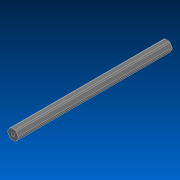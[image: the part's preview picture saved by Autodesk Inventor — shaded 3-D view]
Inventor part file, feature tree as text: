
AUTODESK INVENTOR PART (.ipt)
format: ipt  version: 2022.2 (Build 262287000, 287)  size: 122,368 bytes
history: native  units: in
note: dims shown in document units (in); Inventor stores cm internally (conversion verified against a paired STEP export)
features: extrude x1, sketch x1, other x1
ambient origin geometry x8: Origin, YZ Plane, XZ Plane, XY Plane, X Axis, Y Axis, Z Axis, Center Point
bodies: Solid1 (feature_tree)
feature tree (3):
  extrude  "Extrusion1"  TaperAngle=0.0deg  [1 undecoded]
  sketch  "Sketch1"  dims[d0=28.0in d1=0.0in]
  other  "Cut-Extrude2"
note: 1 required parameter value undecoded (feature->parameter linkage not recoverable at this tier; creation-order binding heuristic only, values carry confidence <= 0.55)
